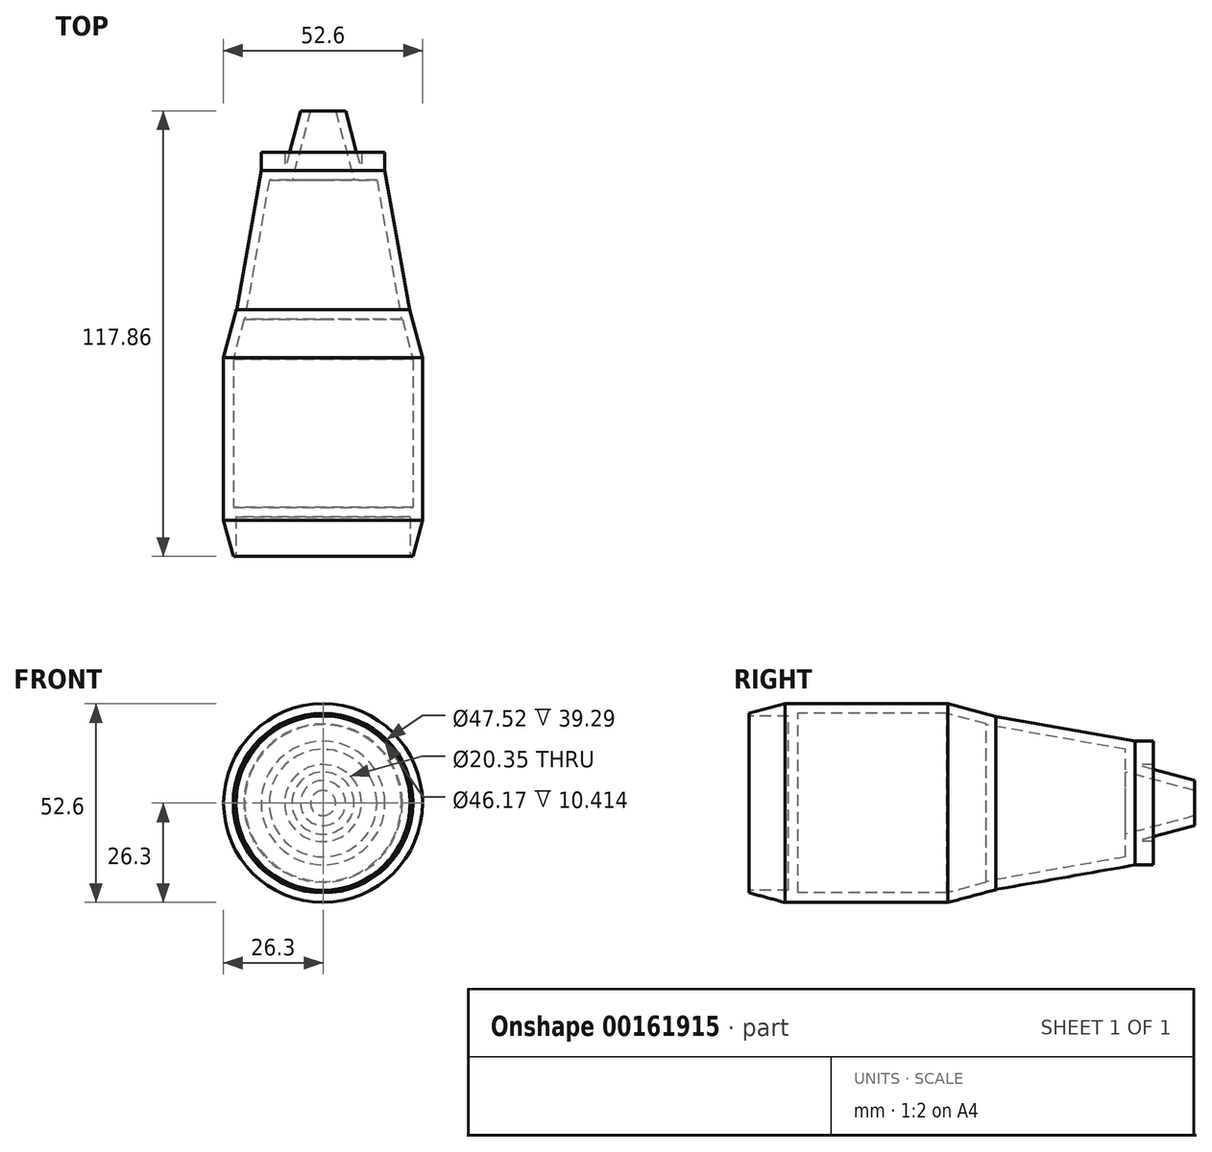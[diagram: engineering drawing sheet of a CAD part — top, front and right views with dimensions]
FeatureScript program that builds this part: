
annotation { "Feature Type Name" : "Feature", "Feature Type Description" : "" }
export const myFeature = defineFeature(function(context is Context, id is Id, definition is map)
    precondition{}
    {
        {
            var Q0;
            Q0=qCreatedBy(makeId("Front.planeOp"),FACE);
            var sketch = newSketch(context, id + "F0", { "sketchPlane" : qUnion([Q0])});
            skCircle(sketch, "E0", {"center": v(0, 0) * mm, "radius": 26.3 * mm});
            skCircle(sketch, "E1", {"center": v(0, 0) * mm, "radius": 23.08 * mm});
            skSolve(sketch);
        }
        {
            var Q0;
            Q0=makeQuery(id+"F0.imprint","IMPRINT",FACE,{"disambiguationData":[TD([[makeQuery(id+"F0.imprint","IMPRINT",EDGE,{"derivedFrom":sQuery(id+"F0.wireOp",EDGE,"E0")}),1.0]])]});
            extrude(context, id + "F1", {"entities" : qUnion([Q0]), "oppositeDirection" : true, "depth" : 39.88 * mm, "hasSecondDirection" : true, "secondDirectionOppositeDirection" : false, "secondDirectionDepth" : 25.4 * mm});
        }
        {
            var Q0;
            Q0=makeQuery(id+"F0.imprint","IMPRINT",FACE,{"disambiguationData":[TD([[makeQuery(id+"F0.imprint","IMPRINT",EDGE,{"derivedFrom":sQuery(id+"F0.wireOp",EDGE,"E1")}),1.0]])]});
            extrude(context, id + "F2", {"entities" : qUnion([Q0]), "operationType" : NewBodyOperationType.ADD, "depth" : 15 * mm});
        }
        {
            var Q0;
            Q0=makeQuery(id+"F0.imprint","IMPRINT",FACE,{"disambiguationData":[TD([[makeQuery(id+"F0.imprint","IMPRINT",EDGE,{"derivedFrom":sQuery(id+"F0.wireOp",EDGE,"E1")}),1.0]])]});
            extrude(context, id + "F3", {"entities" : qUnion([Q0]), "operationType" : NewBodyOperationType.ADD, "oppositeDirection" : true, "depth" : 76.7 * mm});
        }
        {
            var Q0;
            Q0=makeQuery(id+"F3.opExtrude","CAP_EDGE",EDGE,{"disambiguationData":[OSD([sQuery(id+"F0.wireOp",EDGE,"E1")])],"isStart":false});
            chamfer(context, id + "F4", {"entities" : qUnion([Q0]), "chamferType" : ChamferType.OFFSET_ANGLE, "width" : 38.1 * mm, "oppositeDirection" : false, "angle" : 10 * degree, "tangentPropagation" : true});
        }
        {
            var Q0;
            Q0=makeQuery(id+"F1.opExtrude","CAP_EDGE",EDGE,{"disambiguationData":[OSD([sQuery(id+"F0.wireOp",EDGE,"E0")])],"isStart":false});
            chamfer(context, id + "F5", {"entities" : qUnion([Q0]), "chamferType" : ChamferType.OFFSET_ANGLE, "width" : 12.7 * mm, "oppositeDirection" : false, "angle" : 15 * degree, "tangentPropagation" : true});
        }
        {
            var Q0;
            Q0=makeQuery(id+"F1.opExtrude","CAP_EDGE",EDGE,{"disambiguationData":[OSD([sQuery(id+"F0.wireOp",EDGE,"E0")])],"isStart":true});
            chamfer(context, id + "F6", {"entities" : qUnion([Q0]), "chamferType" : ChamferType.OFFSET_ANGLE, "width" : 2.54 * mm, "oppositeDirection" : false, "angle" : 75 * degree, "tangentPropagation" : true});
        }
        {
            var Q0;
            Q0=makeQuery(id+"F3.opExtrude","CAP_FACE",FACE,{"disambiguationData":[OSD([sQuery(id+"F0.wireOp",EDGE,"E1")])],"isStart":false});
            var sketch = newSketch(context, id + "F7", { "sketchPlane" : qUnion([Q0])});
            skCircle(sketch, "E2", {"center": v(0, 0) * mm, "radius": 13.57 * mm});
            skSolve(sketch);
        }
        {
            var Q0;
            Q0=makeQuery(id+"F7.imprint","IMPRINT",FACE,{"disambiguationData":[TD([[makeQuery(id+"F7.imprint","IMPRINT",EDGE,{"derivedFrom":sQuery(id+"F7.wireOp",EDGE,"E2")}),1.0]])]});
            extrude(context, id + "F8", {"entities" : qUnion([Q0]), "operationType" : NewBodyOperationType.ADD, "depth" : 15.75 * mm});
        }
        {
            var Q0;
            Q0=makeQuery(id+"F8.opExtrude","CAP_EDGE",EDGE,{"disambiguationData":[OSD([sQuery(id+"F7.wireOp",EDGE,"E2")])],"isStart":false});
            chamfer(context, id + "F9", {"entities" : qUnion([Q0]), "chamferType" : ChamferType.OFFSET_ANGLE, "width" : 7.62 * mm, "oppositeDirection" : false, "angle" : 75 * degree, "tangentPropagation" : true});
        }
        {
            var Q0;
            Q0=makeQuery(id+"F8.opExtrude","CAP_FACE",FACE,{"disambiguationData":[OSD([sQuery(id+"F7.wireOp",EDGE,"E2")])],"isStart":false});
            shell(context, id + "F10", {"entities" : qUnion([Q0]), "thickness" : 2.54 * mm});
        }
        {
            var Q0;
            Q0=makeQuery(id+"F3.opExtrude","CAP_FACE",FACE,{"disambiguationData":[OSD([sQuery(id+"F0.wireOp",EDGE,"E1")])],"isStart":false});
            extrude(context, id + "F11", {"entities" : qUnion([Q0]), "operationType" : NewBodyOperationType.ADD, "depth" : 4.83 * mm});
        }
    });
